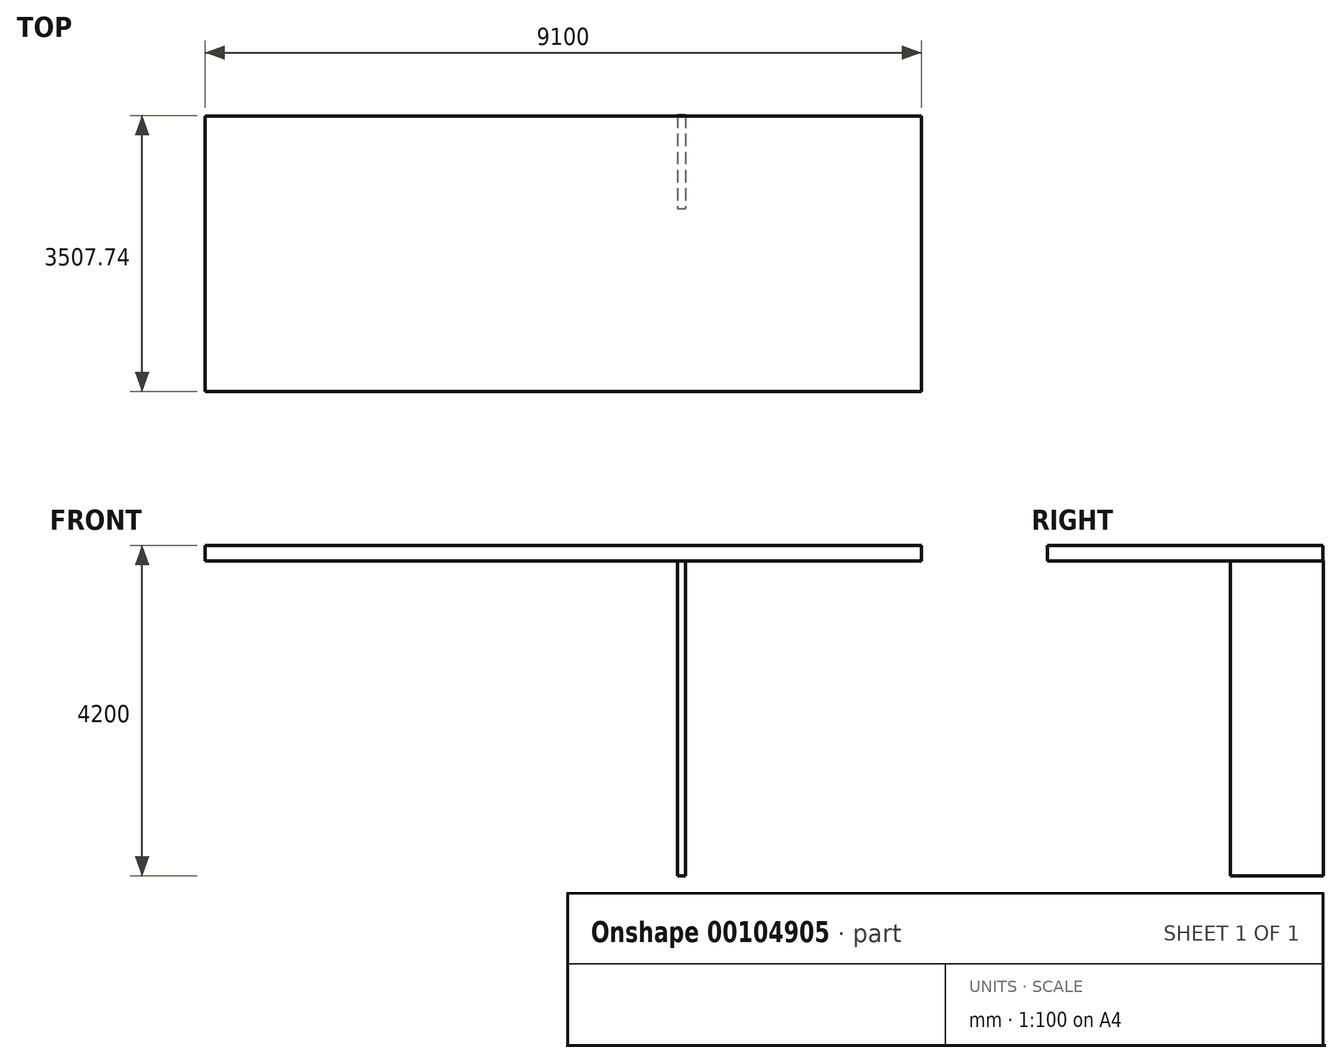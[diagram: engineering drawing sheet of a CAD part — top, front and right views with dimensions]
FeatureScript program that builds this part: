
annotation { "Feature Type Name" : "Feature", "Feature Type Description" : "" }
export const myFeature = defineFeature(function(context is Context, id is Id, definition is map)
    precondition{}
    {
        {
            var Q0;
            Q0=qCreatedBy(makeId("Top.planeOp"),FACE);
            var sketch = newSketch(context, id + "F0", { "sketchPlane" : qUnion([Q0])});
            skLineSegment(sketch, "E0.bottom", {"start": v(-3807.43, 2241.5) * mm, "end": v(5292.57, 2241.5) * mm});
            skLineSegment(sketch, "E0.top", {"start": v(-3807.43, -1258.5) * mm, "end": v(5292.57, -1258.5) * mm});
            skLineSegment(sketch, "E0.left", {"start": v(-3807.43, 2241.5) * mm, "end": v(-3807.43, -1258.5) * mm});
            skLineSegment(sketch, "E0.right", {"start": v(5292.57, 2241.5) * mm, "end": v(5292.57, -1258.5) * mm});
            skSolve(sketch);
        }
        {
            var Q0;
            Q0=qSketchRegion(id+"F0",true);
            extrude(context, id + "F1", {"entities" : qUnion([Q0]), "depth" : 200 * mm});
        }
        {
            var Q0;
            Q0=qCreatedBy(makeId("Top.planeOp"),FACE);
            var sketch = newSketch(context, id + "F2", { "sketchPlane" : qUnion([Q0])});
            skLineSegment(sketch, "E1.bottom", {"start": v(2190.64, 2249.25) * mm, "end": v(2298.12, 2249.25) * mm});
            skLineSegment(sketch, "E1.top", {"start": v(2190.64, 1068.2) * mm, "end": v(2298.12, 1068.2) * mm});
            skLineSegment(sketch, "E1.left", {"start": v(2190.64, 2249.25) * mm, "end": v(2190.64, 1068.2) * mm});
            skLineSegment(sketch, "E1.right", {"start": v(2298.12, 2249.25) * mm, "end": v(2298.12, 1068.2) * mm});
            skSolve(sketch);
        }
        {
            var Q0;
            Q0=qSketchRegion(id+"F2",true);
            extrude(context, id + "F3", {"entities" : qUnion([Q0]), "oppositeDirection" : true, "depth" : 4000 * mm});
        }
    });
